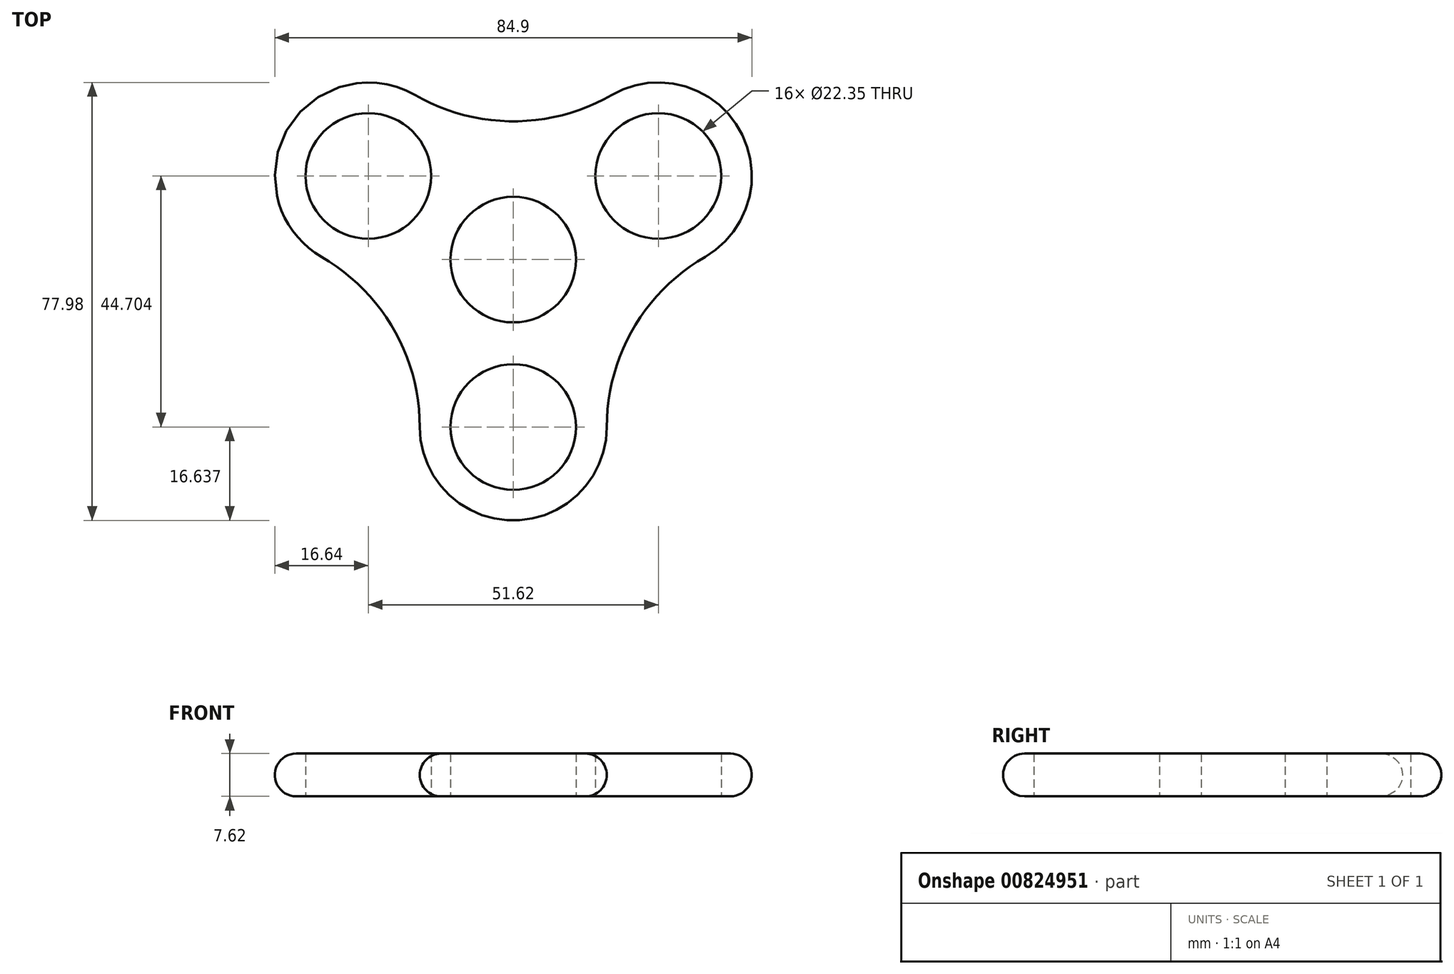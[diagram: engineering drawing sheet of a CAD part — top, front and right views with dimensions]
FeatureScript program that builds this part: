
annotation { "Feature Type Name" : "Feature", "Feature Type Description" : "" }
export const myFeature = defineFeature(function(context is Context, id is Id, definition is map)
    precondition{}
    {
        {
            var Q0;
            Q0=qCreatedBy(makeId("Top.planeOp"),FACE);
            var sketch = newSketch(context, id + "F0", { "sketchPlane" : qUnion([Q0])});
            skPoint(sketch, "E0.center", {"position": v(0, 0) * mm});
            skCircle(sketch, "E1", {"center": v(-25.8, 14.9) * mm, "radius": 11.18 * mm});
            skCircle(sketch, "E2", {"center": v(0, 0) * mm, "radius": 11.18 * mm});
            skCircle(sketch, "E3.1.0", {"center": v(0, -29.8) * mm, "radius": 11.18 * mm});
            skCircle(sketch, "E3.2.0", {"center": v(25.8, 14.9) * mm, "radius": 11.18 * mm});
            skPoint(sketch, "E4.middle", {"position": v(0, -14.9) * mm});
            skPoint(sketch, "E5.orphan", {"position": v(13.66, 0) * mm});
            skArc(sketch, "E6.0", {"start": v(-17.49, 29.31) * mm, "mid": v(-40.22, 23.22) * mm, "end": v(-34.13, 0.5) * mm});
            skArc(sketch, "E6.1", {"start": v(34.13, 0.5) * mm, "mid": v(40.22, 23.22) * mm, "end": v(17.49, 29.31) * mm});
            skArc(sketch, "E6.2", {"start": v(34.13, 0.5) * mm, "mid": v(21.33, -12.31) * mm, "end": v(16.64, -29.8) * mm});
            skArc(sketch, "E6.3", {"start": v(-17.49, 29.31) * mm, "mid": v(0, 24.63) * mm, "end": v(17.49, 29.31) * mm});
            skArc(sketch, "E6.4", {"start": v(-16.64, -29.8) * mm, "mid": v(0, -46.44) * mm, "end": v(16.64, -29.8) * mm});
            skArc(sketch, "E6.5", {"start": v(-16.64, -29.8) * mm, "mid": v(-21.33, -12.31) * mm, "end": v(-34.13, 0.5) * mm});
            skSolve(sketch);
        }
        {
            var Q0;
            Q0=qSketchRegion(id+"F0",true);
            var Q1;
            {var subQ1=sQuery(id+"F0.wireOp",EDGE,"VKsS3Otb-miZj-gkGU-12GB-d8zIMCj1J9sK");var subQ7=makeQuery(id+"F0.imprint","INTERSECT",VERTEX,{"derivedFrom":[subQ1,sQuery(id+"F0.wireOp",EDGE,"2a81f7ea-dfaa-4220-9730-6b88422f781c.2.0")]});Q1=makeQuery(id+"F0.imprint","IMPRINT",FACE,{"disambiguationData":[TD([[makeQuery(id+"F0.imprint","IMPRINT",EDGE,{"disambiguationData":[TD([[subQ7,-1.0]])],"derivedFrom":subQ1}),1.0]])]});}
            var Q2;
            {var subQ3=sQuery(id+"F0.wireOp",EDGE,"2b8rqVyu-uKhq-1D1T-Kwuw-1NqnRaVyucTM");var subQ5=sQuery(id+"F0.wireOp",EDGE,"E2");var subQ6=makeQuery(id+"F0.imprint","INTERSECT",VERTEX,{"derivedFrom":[subQ5,subQ3]});Q2=makeQuery(id+"F0.imprint","IMPRINT",FACE,{"disambiguationData":[TD([[makeQuery(id+"F0.imprint","IMPRINT",EDGE,{"disambiguationData":[TD([[subQ6,-1.0]])],"derivedFrom":subQ5}),-1.0]])]});}
            var Q3;
            {var subQ5=sQuery(id+"F0.wireOp",EDGE,"VKsS3Otb-miZj-gkGU-12GB-d8zIMCj1J9sK");var subQ8=makeQuery(id+"F0.imprint","INTERSECT",VERTEX,{"derivedFrom":[subQ5,sQuery(id+"F0.wireOp",EDGE,"ad422b94-503c-4b8c-a564-e47813131238.2.1")]});Q3=makeQuery(id+"F0.imprint","IMPRINT",FACE,{"disambiguationData":[TD([[makeQuery(id+"F0.imprint","IMPRINT",EDGE,{"disambiguationData":[TD([[subQ8,1.0]])],"derivedFrom":subQ5}),1.0]])]});}
            var Q4;
            {var subQ3=sQuery(id+"F0.wireOp",EDGE,"KG0W6A2v-qbmV-kile-noT2-Lh5GOKsosSiX");var subQ5=sQuery(id+"F0.wireOp",EDGE,"E2");var subQ6=makeQuery(id+"F0.imprint","INTERSECT",VERTEX,{"derivedFrom":[subQ5,subQ3]});Q4=makeQuery(id+"F0.imprint","IMPRINT",FACE,{"disambiguationData":[TD([[makeQuery(id+"F0.imprint","IMPRINT",EDGE,{"disambiguationData":[TD([[subQ6,1.0]])],"derivedFrom":subQ5}),-1.0]])]});}
            var Q5;
            {var subQ1=sQuery(id+"F0.wireOp",EDGE,"VKsS3Otb-miZj-gkGU-12GB-d8zIMCj1J9sK");var subQ7=makeQuery(id+"F0.imprint","INTERSECT",VERTEX,{"derivedFrom":[subQ1,sQuery(id+"F0.wireOp",EDGE,"ad422b94-503c-4b8c-a564-e47813131238.1.1")]});Q5=makeQuery(id+"F0.imprint","IMPRINT",FACE,{"disambiguationData":[TD([[makeQuery(id+"F0.imprint","IMPRINT",EDGE,{"disambiguationData":[TD([[subQ7,1.0]])],"derivedFrom":subQ1}),1.0]])]});}
            extrude(context, id + "F1", {"entities" : qUnion([Q0, Q1, Q2, Q3, Q4, Q5]), "depth" : 7.62 * mm, "offsetDistance" : 25.4 * mm});
        }
        {
            var Q0;
            Q0=makeQuery(id+"F1.opExtrude","CAP_EDGE",EDGE,{"disambiguationData":[OSD([sQuery(id+"F0.wireOp",EDGE,"E6.5")])],"isStart":false});
            var Q1;
            Q1=makeQuery(id+"F1.opExtrude","CAP_EDGE",EDGE,{"disambiguationData":[OSD([sQuery(id+"F0.wireOp",EDGE,"E6.4")])],"isStart":true});
            fillet(context, id + "F2", {"entities" : qUnion([Q0, Q1]), "radius" : 3.8 * mm, "tangentPropagation" : true, "allowEdgeOverflow" : false});
        }
    });
